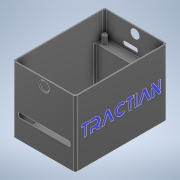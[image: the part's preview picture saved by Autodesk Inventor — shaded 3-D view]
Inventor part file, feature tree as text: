
AUTODESK INVENTOR PART (.ipt)
format: ipt  version: 2021 (Build 250183000, 183)  size: 398,848 bytes
history: native  units: mm
features: sketch x12, extrude x10, other x3, fillet x3, hole x2
ambient origin geometry x8: Origin, YZ Plane, XZ Plane, XY Plane, X Axis, Y Axis, Z Axis, Center Point
bodies: Body1 (feature_tree)
feature tree (30):
  other  "Sólido1"
  extrude  "Extrusão1"  Depth=53.0mm
  extrude  "Extrusão2"  Depth=0.5mm
  extrude  "Extrusão3"  Depth=11.0mm
  fillet  "Arredondamento1"  Radius=19.5mm
  extrude  "Extrusão4"  Depth=2.5mm
  extrude  "Extrusão5"  Depth=1.0mm
  extrude  "Extrusão6"  Depth=31.5mm
  extrude  "Extrusão7"  Depth=23.0mm
  extrude  "Extrusão8"  Depth=2.5mm
  fillet  "Arredondamento3"  Radius=2.5mm
  fillet  "Arredondamento4"  Radius=24.5mm
  extrude  "Extrusão9"  Depth=11.0mm
  hole  "Furo1"  [1 undecoded]
  hole  "Furo2"  [1 undecoded]
  extrude  "Extrusão10"  Depth=5.0mm TaperAngle=0.0deg
  sketch  "Esboço1"  dims[d0=100.0mm d1=53.0mm]
  sketch  "Esboço2"  dims[d2=30.0mm d3=0.0mm d4=0.5mm]
  other  "Contorno projetado1"
  sketch  "Esboço3"  dims[d5=29.5mm d6=0.0mm d7=11.0mm d8=19.5mm]
  sketch  "Esboço4"  dims[d9=2.5mm d10=2.5mm]
  sketch  "Esboço5"  dims[d11=4.5mm d12=0.0mm d13=1.0mm]
  sketch  "Esboço6"  dims[d15=5.5mm d16=31.5mm]
  sketch  "Esboço7"  dims[d17=23.0mm d18=0.0mm d19=3.421mm]
  sketch  "Esboço8"  dims[d20=3.5mm d21=2.5mm d22=2.5mm d23=24.5mm]
  sketch  "Esboço9"  dims[d24=5.0mm d25=0.0mm d26=11.0mm]
  other  "Contorno projetado2"
  sketch  "Esboço10"  dims[d27=14.0mm d28=30.0mm]
  sketch  "Esboço11"  dims[d29=3.0mm d30=5.0mm d31=0.0mm]
  sketch  "Esboço12"  dims[d32=3.0mm d33=5.0mm d34=0.0mm d35=0.5mm d36=5.0mm d37=0.0mm d38=1.0mm d39=1.0mm d40=8.0mm d41=0.0mm d42=4.0mm d43=3.0mm d44=6.0mm d45=6.0mm d46=2.0mm d47=90.0deg d48=8.0mm d49=20.594885mm d50=3.0mm d51=6.0mm d52=6.0mm d53=2.0mm d54=90.0deg d55=8.0mm d56=20.594885mm d57=1.5mm d58=1.5mm d59=1.5mm d60=1.5mm d61=5.5mm d62=15.0mm d64=0.5mm d65=3.0mm d66=3.0mm d67=1.5mm d68=1.5mm d71=1.5mm d72=3.0mm d73=1.5mm d74=1.5mm d75=1.5mm d76=0.5mm d80=4.0mm d81=2.0mm d82=7.0mm d83=0.5mm d84=1.5mm d85=90.0deg d86=45.0deg d87=1.5mm d89=1.5mm d90=1.5mm d91=1.5mm d92=1.5mm d94=0.5mm d95=1.5mm d96=0.5mm d97=1.5mm d98=4.0mm d99=2.0mm d100=1.5mm d101=1.5mm d102=0.5mm d103=0.5mm d104=1.5mm d105=0.5mm d106=1.5mm d108=6.108652mm d109=1.5mm d110=0.5mm d111=0.25mm d112=0.0mm d113=2.564mm d114=1.0mm d115=1.0mm]
note: 2 required parameter values undecoded (feature->parameter linkage not recoverable at this tier; creation-order binding heuristic only, values carry confidence <= 0.55)
